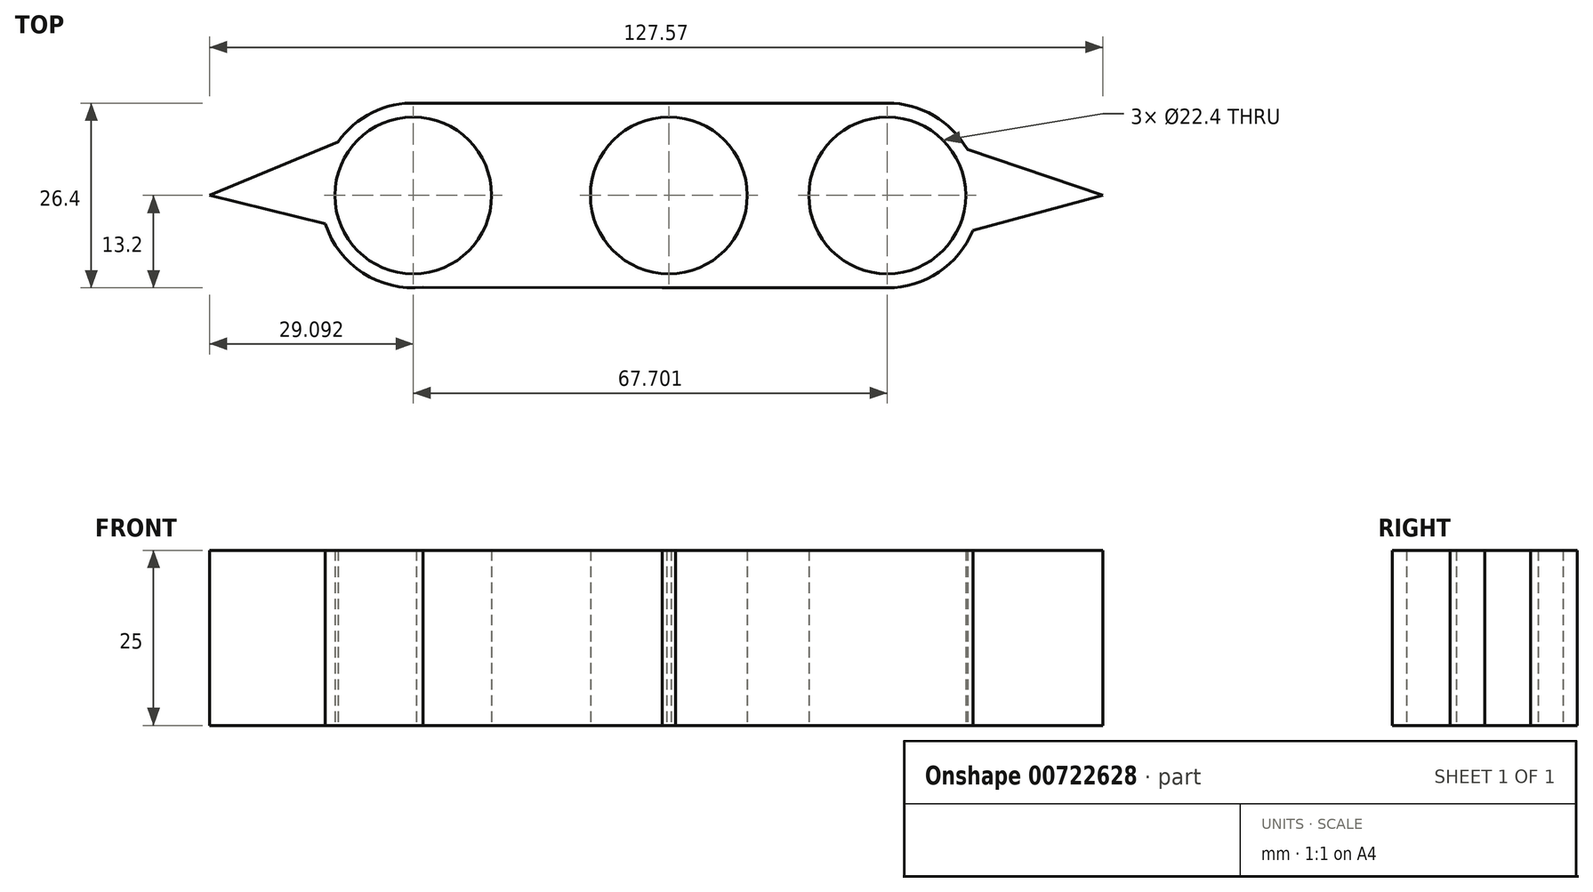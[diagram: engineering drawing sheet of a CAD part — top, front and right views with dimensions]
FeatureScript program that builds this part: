
annotation { "Feature Type Name" : "Feature", "Feature Type Description" : "" }
export const myFeature = defineFeature(function(context is Context, id is Id, definition is map)
    precondition{}
    {
        {
            var Q0;
            Q0=qCreatedBy(makeId("Top.planeOp"),FACE);
            var sketch = newSketch(context, id + "F0", { "sketchPlane" : qUnion([Q0])});
            skCircle(sketch, "E0", {"center": v(0, 0) * mm, "radius": 11.2 * mm});
            skCircle(sketch, "E1", {"center": v(0, 0) * mm, "radius": 13.2 * mm});
            skCircle(sketch, "E2", {"center": v(-36.5, 0) * mm, "radius": 11.2 * mm});
            skArc(sketch, "E3", {"start": v(-36.07, 13.2) * mm, "mid": v(-49.7, -0.48) * mm, "end": v(-35.1, -13.13) * mm});
            skCircle(sketch, "E4", {"center": v(31.2, 0) * mm, "radius": 11.2 * mm});
            skArc(sketch, "E5", {"start": v(31.18, -13.2) * mm, "mid": v(44.4, 0) * mm, "end": v(31.2, 13.2) * mm});
            skLineSegment(sketch, "E6", {"start": v(-36.95, 13.2) * mm, "end": v(31.2, 13.2) * mm});
            skLineSegment(sketch, "E7", {"start": v(-35.1, -13.13) * mm, "end": v(31.18, -13.2) * mm});
            skLineSegment(sketch, "E8", {"start": v(-49.07, -4.05) * mm, "end": v(-65.6, 0) * mm});
            skLineSegment(sketch, "E9", {"start": v(-65.6, 0) * mm, "end": v(-47.27, 7.65) * mm});
            skLineSegment(sketch, "E10", {"start": v(43.42, -4.98) * mm, "end": v(61.97, 0) * mm});
            skLineSegment(sketch, "E11", {"start": v(61.97, 0) * mm, "end": v(42.66, 6.54) * mm});
            skSolve(sketch);
        }
        {
            var Q0;
            Q0 = qSketchRegion(id + "F0", true);
            extrude(context, id + "F1", {"entities" : qUnion([Q0]), "depth" : 25 * mm, "offsetDistance" : 25 * mm});
        }
    });
